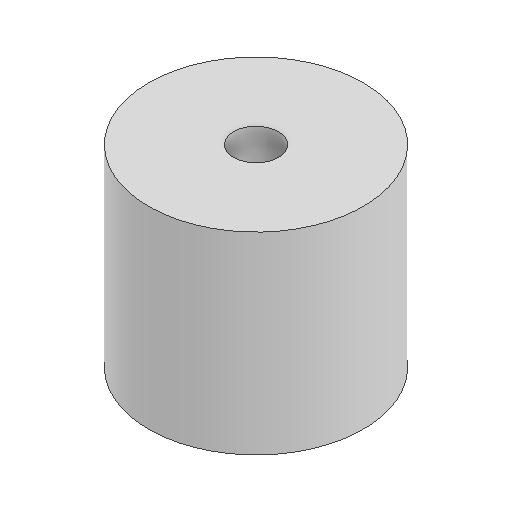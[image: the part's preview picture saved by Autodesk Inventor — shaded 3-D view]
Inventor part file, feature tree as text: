
AUTODESK INVENTOR PART (.ipt)
format: ipt  version: 2025 (Build 290162000, 162)  size: 86,528 bytes
history: native  units: in
note: dims shown in document units (in); Inventor stores cm internally (conversion verified against a paired STEP export)
features: extrude x1, sketch x1
ambient origin geometry x8: Origin, YZ Plane, XZ Plane, XY Plane, X Axis, Y Axis, Z Axis, Center Point
bodies: Solid1 (feature_tree)
feature tree (2):
  extrude  "Extrusion1"  Depth=0.9in
  sketch  "Sketch1"  dims[d0=0.209in d1=1.0in d2=0.9in d3=0.0in]
